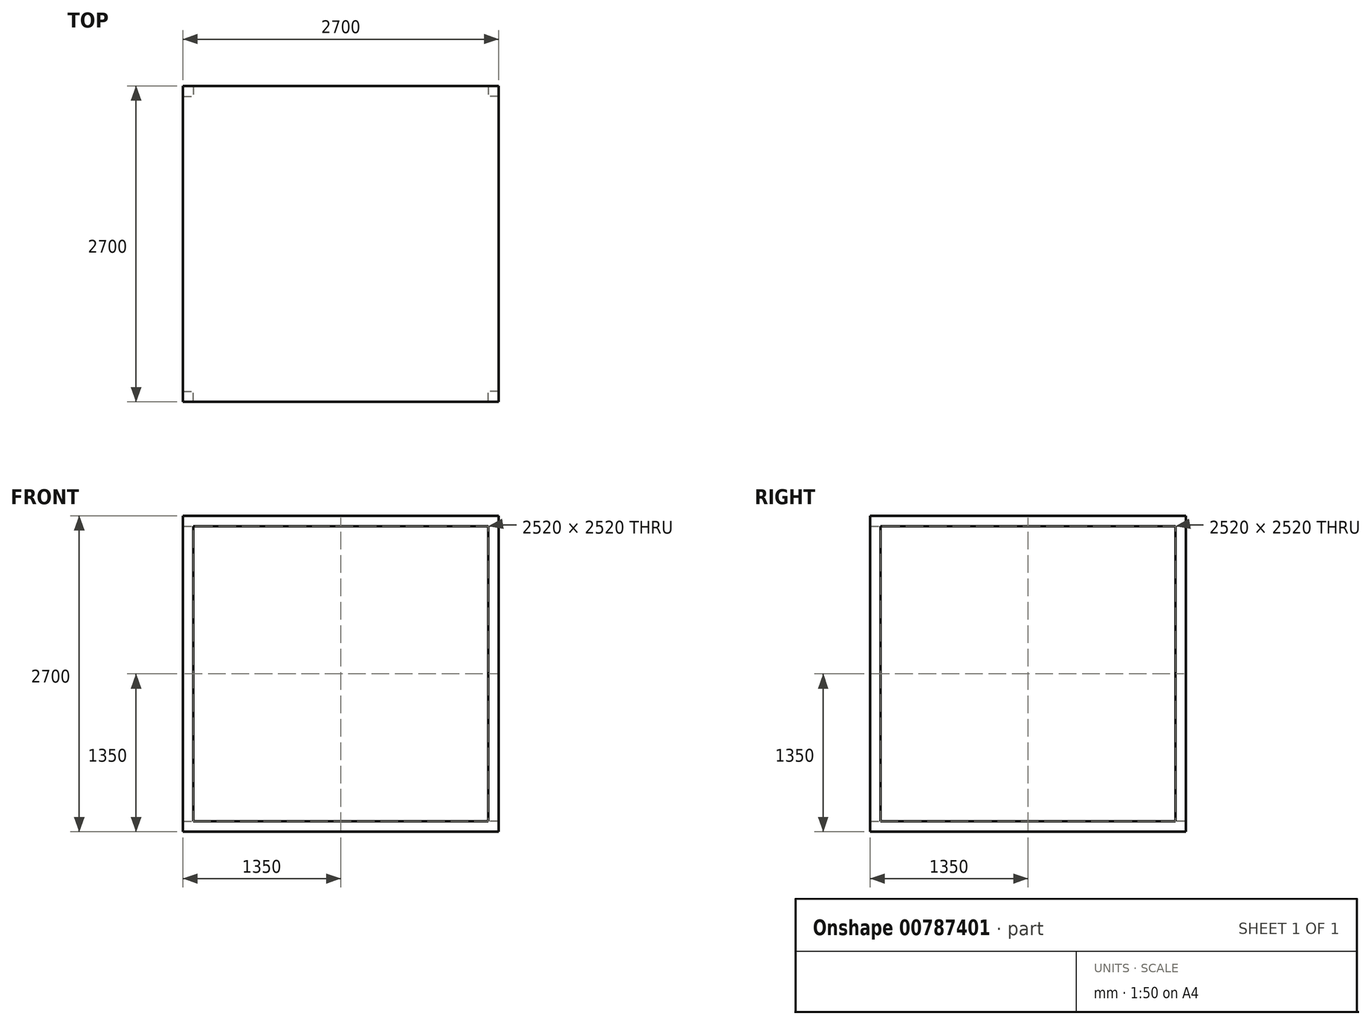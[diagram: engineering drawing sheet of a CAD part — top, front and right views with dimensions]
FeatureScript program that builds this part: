
annotation { "Feature Type Name" : "Feature", "Feature Type Description" : "" }
export const myFeature = defineFeature(function(context is Context, id is Id, definition is map)
    precondition{}
    {
        {
            var Q0;
            Q0=qCreatedBy(makeId("Top.planeOp"),FACE);
            var sketch = newSketch(context, id + "F0", { "sketchPlane" : qUnion([Q0])});
            skLineSegment(sketch, "E0.bottom", {"start": v(1350, 1350) * mm, "end": v(-1350, 1350) * mm});
            skLineSegment(sketch, "E0.top", {"start": v(1350, -1350) * mm, "end": v(-1350, -1350) * mm});
            skLineSegment(sketch, "E0.left", {"start": v(1350, 1350) * mm, "end": v(1350, -1350) * mm});
            skLineSegment(sketch, "E0.right", {"start": v(-1350, 1350) * mm, "end": v(-1350, -1350) * mm});
            skPoint(sketch, "E0.middle", {"position": v(0, 0) * mm});
            skSolve(sketch);
        }
        {
            var Q0;
            Q0 = qSketchRegion(id + "F0", true);
            extrude(context, id + "F1", {"entities" : qUnion([Q0]), "depth" : 90 * mm, "offsetDistance" : 25 * mm});
        }
        {
            var Q0;
            Q0=makeQuery(id+"F1.opExtrude","CAP_FACE",FACE,{"disambiguationData":[OSD([sQuery(id+"F0.wireOp",EDGE,"E0.bottom"),sQuery(id+"F0.wireOp",EDGE,"E0.top"),sQuery(id+"F0.wireOp",EDGE,"E0.left"),sQuery(id+"F0.wireOp",EDGE,"E0.right")])],"isStart":false});
            var sketch = newSketch(context, id + "F2", { "sketchPlane" : qUnion([Q0])});
            skLineSegment(sketch, "E1.bottom", {"start": v(-1350, -1350) * mm, "end": v(-1260, -1350) * mm});
            skLineSegment(sketch, "E1.top", {"start": v(-1350, -1260) * mm, "end": v(-1260, -1260) * mm});
            skLineSegment(sketch, "E1.left", {"start": v(-1350, -1350) * mm, "end": v(-1350, -1260) * mm});
            skLineSegment(sketch, "E1.right", {"start": v(-1260, -1350) * mm, "end": v(-1260, -1260) * mm});
            skLineSegment(sketch, "E2", {"start": v(0, 0) * mm, "end": v(-1350, 0) * mm, "construction": true});
            skLineSegment(sketch, "E3", {"start": v(0, 0) * mm, "end": v(0, -1350) * mm, "construction": true});
            skLineSegment(sketch, "E4.MirrorCS", {"start": v(1350, -1350) * mm, "end": v(1350, -1260) * mm});
            skLineSegment(sketch, "E5.MirrorCS", {"start": v(1350, -1260) * mm, "end": v(1260, -1260) * mm});
            skLineSegment(sketch, "E6.MirrorCS", {"start": v(1260, -1350) * mm, "end": v(1260, -1260) * mm});
            skLineSegment(sketch, "E7.MirrorCS", {"start": v(1350, -1350) * mm, "end": v(1260, -1350) * mm});
            skLineSegment(sketch, "E8.MirrorCS", {"start": v(1350, 1260) * mm, "end": v(1260, 1260) * mm});
            skLineSegment(sketch, "E9.MirrorCS", {"start": v(1350, 1350) * mm, "end": v(1350, 1260) * mm});
            skLineSegment(sketch, "E10.MirrorCS", {"start": v(1350, 1350) * mm, "end": v(1260, 1350) * mm});
            skLineSegment(sketch, "E11.MirrorCS", {"start": v(1260, 1350) * mm, "end": v(1260, 1260) * mm});
            skLineSegment(sketch, "E12.MirrorCS", {"start": v(-1260, 1350) * mm, "end": v(-1260, 1260) * mm});
            skLineSegment(sketch, "E13.MirrorCS", {"start": v(-1350, 1260) * mm, "end": v(-1260, 1260) * mm});
            skLineSegment(sketch, "E14.MirrorCS", {"start": v(-1350, 1350) * mm, "end": v(-1260, 1350) * mm});
            skLineSegment(sketch, "E15.MirrorCS", {"start": v(-1350, 1350) * mm, "end": v(-1350, 1260) * mm});
            skSolve(sketch);
        }
        {
            var Q0;
            Q0 = qSketchRegion(id + "F2", true);
            extrude(context, id + "F3", {"entities" : qUnion([Q0]), "operationType" : NewBodyOperationType.ADD, "depth" : (2700 - 90) * mm, "offsetDistance" : 25 * mm});
        }
        {
            var Q0;
            Q0=makeQuery(id+"F3.opExtrude","CAP_FACE",FACE,{"disambiguationData":[OSD([sQuery(id+"F2.wireOp",EDGE,"E8.MirrorCS"),sQuery(id+"F2.wireOp",EDGE,"E9.MirrorCS"),sQuery(id+"F2.wireOp",EDGE,"E10.MirrorCS"),sQuery(id+"F2.wireOp",EDGE,"E11.MirrorCS")])],"isStart":false});
            var sketch = newSketch(context, id + "F4", { "sketchPlane" : qUnion([Q0])});
            skLineSegment(sketch, "E16.bottom", {"start": v(1350, 1350) * mm, "end": v(-1350, 1350) * mm});
            skLineSegment(sketch, "E16.top", {"start": v(1350, -1350) * mm, "end": v(-1350, -1350) * mm});
            skLineSegment(sketch, "E16.left", {"start": v(1350, 1350) * mm, "end": v(1350, -1350) * mm});
            skLineSegment(sketch, "E16.right", {"start": v(-1350, 1350) * mm, "end": v(-1350, -1350) * mm});
            skPoint(sketch, "E16.middle", {"position": v(0, 0) * mm});
            skLineSegment(sketch, "E17.bottom", {"start": v(1260, 1260) * mm, "end": v(-1260, 1260) * mm, "construction": true});
            skLineSegment(sketch, "E17.top", {"start": v(1260, -1260) * mm, "end": v(-1260, -1260) * mm, "construction": true});
            skLineSegment(sketch, "E17.left", {"start": v(1260, 1260) * mm, "end": v(1260, -1260) * mm, "construction": true});
            skLineSegment(sketch, "E17.right", {"start": v(-1260, 1260) * mm, "end": v(-1260, -1260) * mm, "construction": true});
            skSolve(sketch);
        }
        {
            var Q0;
            Q0 = qSketchRegion(id + "F4", true);
            extrude(context, id + "F5", {"entities" : qUnion([Q0]), "operationType" : NewBodyOperationType.ADD, "oppositeDirection" : true, "depth" : 90 * mm, "offsetDistance" : 25 * mm});
        }
    });
